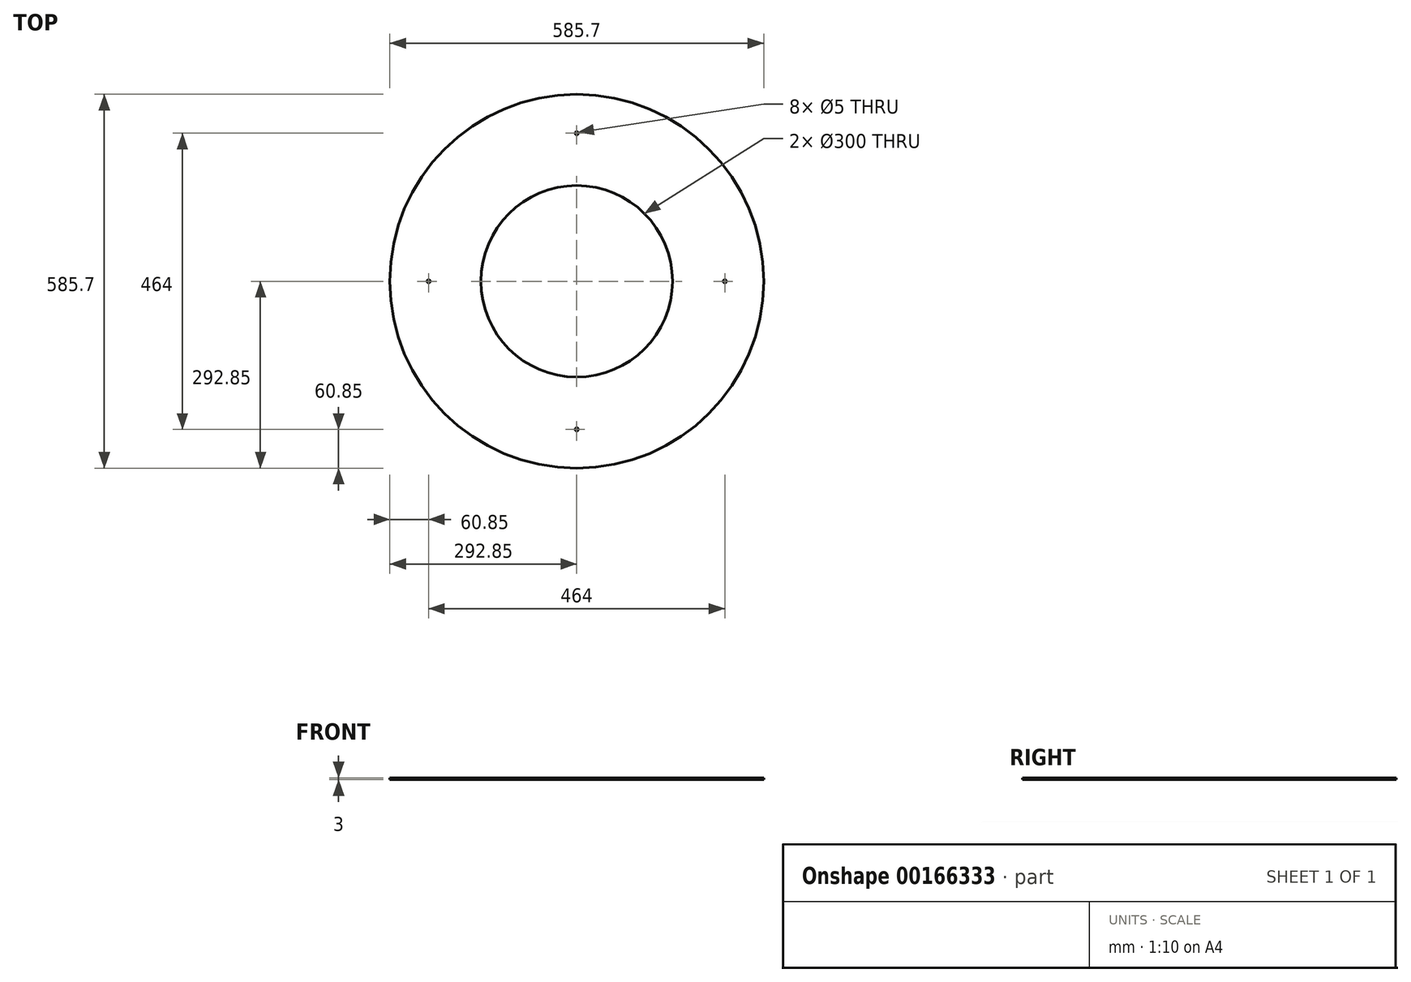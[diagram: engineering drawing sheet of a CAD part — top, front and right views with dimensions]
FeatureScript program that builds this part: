
annotation { "Feature Type Name" : "Feature", "Feature Type Description" : "" }
export const myFeature = defineFeature(function(context is Context, id is Id, definition is map)
    precondition{}
    {
        {
            var Q0;
            Q0=qCreatedBy(makeId("Top.planeOp"),FACE);
            var sketch = newSketch(context, id + "F0", { "sketchPlane" : qUnion([Q0])});
            skCircle(sketch, "E0", {"center": v(0, 0) * mm, "radius": 292.85 * mm});
            skCircle(sketch, "E1", {"center": v(0, 0) * mm, "radius": 150 * mm});
            skSolve(sketch);
        }
        {
            var Q0;
            Q0=makeQuery(id+"F0.imprint","IMPRINT",FACE,{"disambiguationData":[TD([[makeQuery(id+"F0.imprint","IMPRINT",EDGE,{"derivedFrom":sQuery(id+"F0.wireOp",EDGE,"E0")}),1.0]])]});
            extrude(context, id + "F1", {"entities" : qUnion([Q0]), "depth" : 3 * mm});
        }
        {
            var Q0;
            Q0=makeQuery(id+"F1.opExtrude","CAP_FACE",FACE,{"disambiguationData":[OSD([sQuery(id+"F0.wireOp",EDGE,"E0"),sQuery(id+"F0.wireOp",EDGE,"E1")])],"isStart":false});
            var sketch = newSketch(context, id + "F2", { "sketchPlane" : qUnion([Q0])});
            skLineSegment(sketch, "E2", {"start": v(0, 0) * mm, "end": v(0, 232) * mm});
            skCircle(sketch, "E3", {"center": v(0, 232) * mm, "radius": 2.5 * mm});
            skCircle(sketch, "E4.1.0", {"center": v(-232, 0) * mm, "radius": 2.5 * mm});
            skCircle(sketch, "E4.2.0", {"center": v(0, -232) * mm, "radius": 2.5 * mm});
            skCircle(sketch, "E4.3.0", {"center": v(232, 0) * mm, "radius": 2.5 * mm});
            skPoint(sketch, "E4.center", {"position": v(0, 0) * mm});
            skSolve(sketch);
        }
        {
            var Q0;
            Q0=qSketchRegion(id+"F2",true);
            extrude(context, id + "F3", {"entities" : qUnion([Q0]), "operationType" : NewBodyOperationType.REMOVE, "oppositeDirection" : true, "depth" : 3 * mm});
        }
    });
